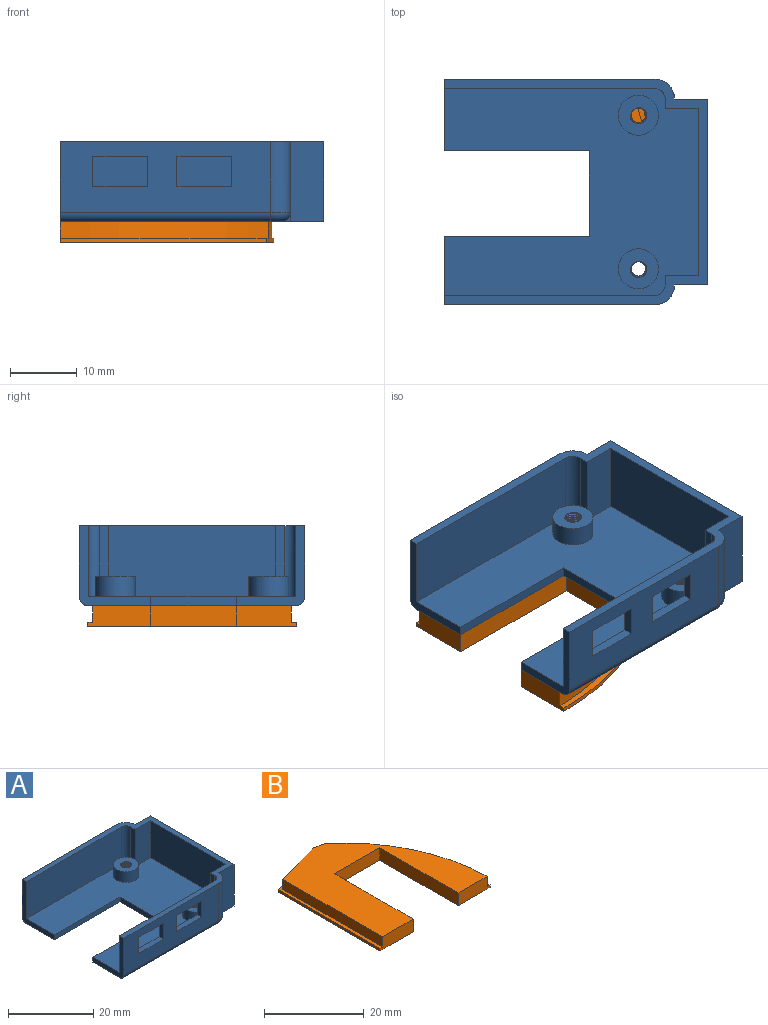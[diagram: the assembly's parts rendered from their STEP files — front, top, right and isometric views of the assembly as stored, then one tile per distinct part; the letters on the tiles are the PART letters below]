
ASSEMBLY  parts=2 mates=1
PART A: 54 faces, bbox 39.6x34.4x12.1 mm
  f0: plane 39.5x31mm, normal (0,0,-1), area 885.2mm2, adj f2,f22,f23,f24,f25,f26,f32,f40
  f1: plane 38.1x31mm, normal (0,0,1), area 815mm2, adj f2,f27,f28,f29,f30,f31,f33,f40
  f2: plane 12x10.28mm, normal (-1,0,0), area 28.8mm2, adj f0,f1,f11,f21,f26,f29,f41
  f3: bspline ~3.21x2.57mm, area 14.6mm2, adj f5,f6,f7,f12
  f4: bspline ~3.21x2.56mm, area 14.6mm2, adj f5,f6,f7,f12,f22
  f5: cylinder r=1.28mm len=2.99mm, axis (0,0,-1), area 5.3mm2, adj f3,f4,f7,f12
  f6: cylinder r=1.09mm len=2.99mm, axis (0,0,1), area 2.5mm2, adj f3,f4,f12,f22
  f7: plane 2.51x2.48mm, normal (0,0,1), area 0.8mm2, adj f3,f4,f5,f22
  f8: cylinder r=3mm len=10.6mm, axis (0,0,1), area 50mm2, adj f11,f21,f23,f48
  f9: cylinder r=3mm len=10.6mm, axis (0,0,1), area 50mm2, adj f10,f21,f24,f49
  f10: plane 31.5x10.6mm, normal (0,1,0), area 333.9mm2, adj f9,f21,f25,f40
  f11: plane 31.5x10.6mm, normal (0,-1,0), area 258.5mm2, adj f2,f8,f13,f14,f15,f16,f17,f18
  f12: plane 6.21x6.1mm, normal (0,0,1), area 23.8mm2, adj f3,f4,f5,f6,f27
  f13: plane 8.2x1.4mm, normal (0,0,-1), area 11.5mm2, adj f11,f14,f16,f29
  f14: plane 4.6x1.4mm, normal (-1,0,0), area 6.4mm2, adj f11,f13,f15,f29
  f15: plane 8.2x1.4mm, normal (0,0,1), area 11.5mm2, adj f11,f14,f16,f29
  f16: plane 4.6x1.4mm, normal (1,0,0), area 6.4mm2, adj f11,f13,f15,f29
  f17: plane 8.2x1.4mm, normal (0,0,-1), area 11.5mm2, adj f11,f18,f20,f29
  f18: plane 4.6x1.4mm, normal (-1,0,0), area 6.4mm2, adj f11,f17,f19,f29
  f19: plane 8.2x1.4mm, normal (0,0,1), area 11.5mm2, adj f11,f18,f20,f29
  f20: plane 4.6x1.4mm, normal (1,0,0), area 6.4mm2, adj f11,f17,f19,f29
  f21: plane 39.5x33.8mm, normal (0,0,1), area 151.2mm2, adj f2,f8,f9,f10,f11,f28,f29,f30
  f22: cone r=1.88mm half-angle=45deg, axis (0,0,-1), area 22.5mm2, adj f0,f4,f6,f7
  f23: torus R=1.6mm, axis (0,0,1), area 8.6mm2, adj f0,f8,f26,f52
  f24: torus R=1.6mm, axis (0,0,1), area 8.6mm2, adj f0,f9,f25,f53
  f25: cylinder r=1.4mm len=31.5mm, axis (1,0,0), area 69.3mm2, adj f0,f10,f24,f40
  f26: cylinder r=1.4mm len=31.5mm, axis (-1,0,0), area 69.3mm2, adj f0,f2,f11,f23
  f27: cylinder r=3mm len=6mm, axis (0,0,1), area 56.5mm2, adj f1,f12
  f28: plane 31.5x10.6mm, normal (0,-1,0), area 333.9mm2, adj f1,f21,f31,f40
  f29: plane 31.5x10.6mm, normal (0,1,0), area 258.5mm2, adj f1,f2,f13,f14,f15,f16,f17,f18
  f30: cylinder r=1.6mm len=10.6mm, axis (0,0,1), area 26.6mm2, adj f1,f21,f29,f47
  f31: cylinder r=1.6mm len=10.6mm, axis (0,0,1), area 26.6mm2, adj f1,f21,f28,f46
  f32: cone r=1.88mm half-angle=45deg, axis (0,0,-1), area 22.5mm2, adj f0,f34,f35,f37
  f33: cylinder r=3mm len=6mm, axis (0,0,1), area 56.5mm2, adj f1,f36
  f34: cylinder r=1.09mm len=2.99mm, axis (0,0,1), area 2.5mm2, adj f32,f36,f37,f38
  f35: plane 2.51x2.5mm, normal (0,0,1), area 0.8mm2, adj f32,f37,f38,f39
  f36: plane 6.1x6.1mm, normal (0,0,1), area 23.8mm2, adj f33,f34,f37,f38,f39
  f37: bspline ~3.21x2.56mm, area 14.6mm2, adj f32,f34,f35,f36,f39
  f38: bspline ~3.21x2.57mm, area 14.6mm2, adj f34,f35,f36,f39
  f39: cylinder r=1.28mm len=2.99mm, axis (0,0,-1), area 5.3mm2, adj f35,f36,f37,f38
  f40: plane 12x10.73mm, normal (-1,0,0), area 29.4mm2, adj f0,f1,f10,f21,f25,f28,f43
  f41: plane 21.77x1.4mm, normal (0,1,0), area 30.5mm2, adj f0,f1,f2,f42
  f42: plane 12.79x1.4mm, normal (-1,0,0), area 17.9mm2, adj f0,f1,f41,f43
  f43: plane 21.77x1.4mm, normal (0,-1,0), area 30.5mm2, adj f0,f1,f40,f42
  f44: plane 10.6x5mm, normal (0,-1,0), area 53mm2, adj f1,f21,f46,f51
  f45: plane 10.6x5mm, normal (0,1,0), area 53mm2, adj f1,f21,f47,f51
  f46: plane 10.6x1.4mm, normal (-1,0,0), area 14.8mm2, adj f1,f21,f31,f44
  f47: plane 10.6x1.4mm, normal (-1,0,0), area 14.8mm2, adj f1,f21,f30,f45
  f48: plane 12x5mm, normal (0,-1,0), area 60mm2, adj f0,f8,f21,f50,f52
  f49: plane 12x5mm, normal (0,1,0), area 60mm2, adj f0,f9,f21,f50,f53
  f50: plane 27.8x12mm, normal (1,0,0), area 333.6mm2, adj f0,f21,f48,f49
  f51: plane 25x10.6mm, normal (-1,0,0), area 265mm2, adj f1,f21,f44,f45
  f52: plane 1.4x1.4mm, normal (0,-1,0), area 0.4mm2, adj f0,f23,f48
  f53: plane 1.4x1.4mm, normal (0,1,0), area 0.4mm2, adj f0,f24,f49
PART B: 16 faces, bbox 31.3x32x3.1 mm
  f0: plane 28.37x2.5mm, normal (-1,0,0), area 70.9mm2, adj f6,f9,f14,f15
  f1: cylinder r=40.72mm len=31.16mm, axis (0,0,-1), area 89.4mm2, adj f8,f11,f13,f15
  f2: plane 22.37x3.1mm, normal (1,0,0), area 69.3mm2, adj f4,f10,f14,f15
  f3: plane 22.37x3.1mm, normal (-1,0,0), area 69.3mm2, adj f4,f10,f13,f15
  f4: plane 31.99x31.28mm, normal (0,0,-1), area 544.4mm2, adj f2,f3,f5,f7,f10,f11,f12,f13
  f5: plane 28.97x0.6mm, normal (-1,0,0), area 17.4mm2, adj f4,f6,f12,f14
  f6: plane 31.99x12.77mm, normal (0,0,1), area 29.3mm2, adj f0,f5,f9,f11,f12,f14
  f7: cylinder r=38.76mm len=30.89mm, axis (0,0,-1), area 21.2mm2, adj f4,f8,f11,f13
  f8: plane 31.16x15.88mm, normal (0,0,1), area 33mm2, adj f1,f7,f11,f13
  f9: plane 12.05x3.32mm, normal (-0.27,0.96,0), area 31.2mm2, adj f0,f6,f11,f15
  f10: plane 12.83x3.1mm, normal (0,-1,0), area 39.8mm2, adj f2,f3,f4,f15
  f11: plane 5.49x3.1mm, normal (0.2,0.98,0), area 10.1mm2, adj f1,f4,f6,f7,f8,f9,f12,f15
  f12: plane 11.28x3.02mm, normal (-0.26,0.97,0), area 7mm2, adj f4,f5,f6,f11
  f13: plane 9.01x3.1mm, normal (0,-1,0), area 25.9mm2, adj f1,f3,f4,f7,f8,f15
  f14: plane 9.44x3.1mm, normal (0,-1,0), area 27.5mm2, adj f0,f2,f4,f5,f6,f15
  f15: plane 31.69x29.74mm, normal (0,0,1), area 482.1mm2, adj f0,f1,f2,f3,f9,f10,f11,f13
PLACE A at identity
PLACE B rot(axis=(0,0,-1),90deg) t=(32.4,-15.25,-3.1)mm
MATE fastened B.f14 <-> A.f40  axis (-1,0,0) through (32.4,-8.83,0)mm
